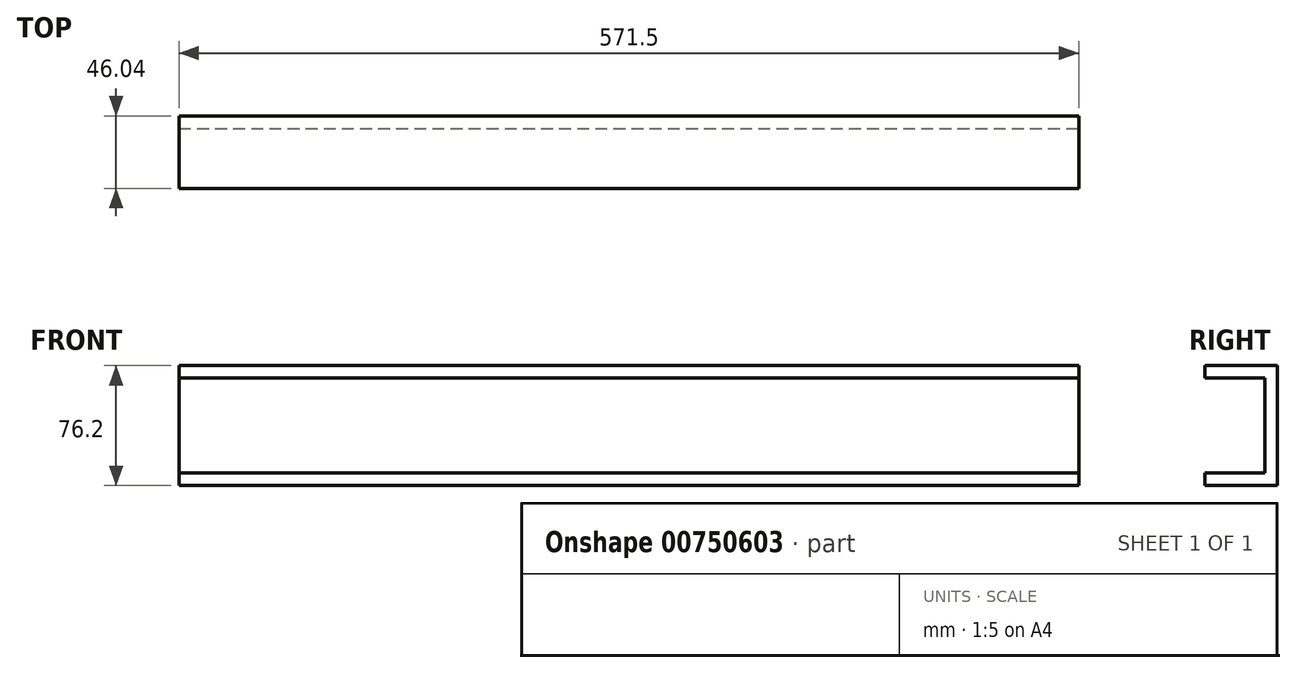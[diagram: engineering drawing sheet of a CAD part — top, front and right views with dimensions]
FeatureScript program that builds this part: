
annotation { "Feature Type Name" : "Feature", "Feature Type Description" : "" }
export const myFeature = defineFeature(function(context is Context, id is Id, definition is map)
    precondition{}
    {
        {
            var Q0;
            Q0=qCreatedBy(makeId("Front.planeOp"),FACE);
            var sketch = newSketch(context, id + "F0", { "sketchPlane" : qUnion([Q0])});
            skLineSegment(sketch, "E0", {"start": v(0, 0) * mm, "end": v(571.5, 0) * mm});
            skLineSegment(sketch, "E1", {"start": v(571.5, 0) * mm, "end": v(571.5, 76.2) * mm});
            skLineSegment(sketch, "E2", {"start": v(571.5, 76.2) * mm, "end": v(0, 76.2) * mm});
            skLineSegment(sketch, "E3", {"start": v(0, 76.2) * mm, "end": v(0, 0) * mm});
            skSolve(sketch);
        }
        {
            var Q0;
            Q0=qSketchRegion(id+"F0",true);
            extrude(context, id + "F1", {"entities" : qUnion([Q0]), "oppositeDirection" : true, "depth" : 7.94 * mm, "offsetDistance" : 25.4 * mm});
        }
        {
            var Q0;
            Q0=qCreatedBy(makeId("Front.planeOp"),FACE);
            var sketch = newSketch(context, id + "F2", { "sketchPlane" : qUnion([Q0])});
            skLineSegment(sketch, "E4.0", {"start": v(571.5, 68.26) * mm, "end": v(0, 68.26) * mm});
            skLineSegment(sketch, "E4.2", {"start": v(0, 7.94) * mm, "end": v(571.5, 7.94) * mm});
            skLineSegment(sketch, "E5.0", {"start": v(571.5, 76.2) * mm, "end": v(0, 76.2) * mm});
            skLineSegment(sketch, "E6.0", {"start": v(0, 0) * mm, "end": v(571.5, 0) * mm});
            skLineSegment(sketch, "E7", {"start": v(0, 76.2) * mm, "end": v(0, 68.26) * mm});
            skLineSegment(sketch, "E8", {"start": v(0, 7.94) * mm, "end": v(0, 0) * mm});
            skLineSegment(sketch, "E9", {"start": v(571.5, 76.2) * mm, "end": v(571.5, 68.26) * mm});
            skLineSegment(sketch, "E10", {"start": v(571.5, 0) * mm, "end": v(571.5, 7.94) * mm});
            skSolve(sketch);
        }
        {
            var Q0;
            Q0 = qSketchRegion(id + "F2", true);
            extrude(context, id + "F3", {"entities" : qUnion([Q0]), "operationType" : NewBodyOperationType.ADD, "depth" : 38.1 * mm, "offsetDistance" : 25.4 * mm});
        }
    });
